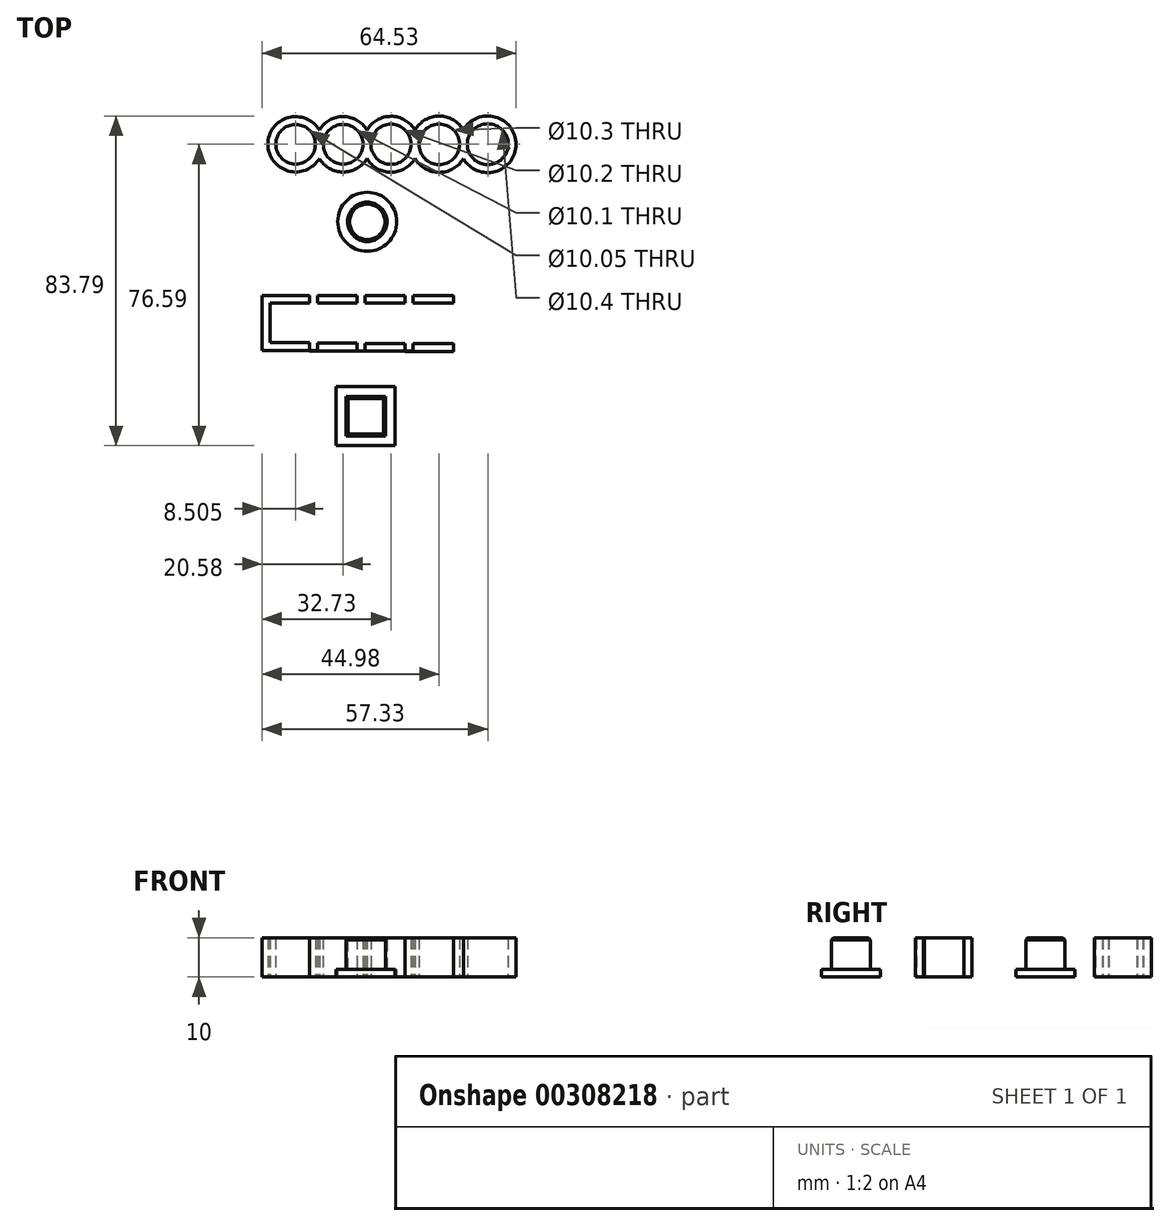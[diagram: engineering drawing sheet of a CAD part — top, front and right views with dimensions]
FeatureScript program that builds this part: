
annotation { "Feature Type Name" : "Feature", "Feature Type Description" : "" }
export const myFeature = defineFeature(function(context is Context, id is Id, definition is map)
    precondition{}
    {
        {
            var Q0;
            Q0=qCreatedBy(makeId("Top.planeOp"),FACE);
            var sketch = newSketch(context, id + "F0", { "sketchPlane" : qUnion([Q0])});
            skLineSegment(sketch, "E0", {"start": v(-24.23, 14.63) * mm, "end": v(24.6, 14.63) * mm, "construction": true});
            skPoint(sketch, "E1", {"position": v(-12.15, 14.63) * mm});
            skPoint(sketch, "E2", {"position": v(0, 14.63) * mm});
            skPoint(sketch, "E3", {"position": v(12.25, 14.63) * mm});
            skCircle(sketch, "E4", {"center": v(-24.23, 14.63) * mm, "radius": 5.03 * mm});
            skCircle(sketch, "E5", {"center": v(24.6, 14.63) * mm, "radius": 5.2 * mm});
            skCircle(sketch, "E6", {"center": v(-12.15, 14.63) * mm, "radius": 5.05 * mm});
            skCircle(sketch, "E7", {"center": v(0, 14.63) * mm, "radius": 5.1 * mm});
            skCircle(sketch, "E8", {"center": v(12.25, 14.63) * mm, "radius": 5.15 * mm});
            skCircle(sketch, "E9", {"center": v(-24.23, 14.63) * mm, "radius": 7.03 * mm});
            skCircle(sketch, "E10", {"center": v(-12.15, 14.63) * mm, "radius": 7.05 * mm});
            skCircle(sketch, "E11", {"center": v(0, 14.63) * mm, "radius": 7.1 * mm});
            skCircle(sketch, "E12", {"center": v(12.25, 14.63) * mm, "radius": 7.15 * mm});
            skCircle(sketch, "E13", {"center": v(24.6, 14.63) * mm, "radius": 7.2 * mm});
            skCircle(sketch, "E14", {"center": v(-6.02, -5.07) * mm, "radius": 7.5 * mm});
            skCircle(sketch, "E15", {"center": v(-6.02, -5.07) * mm, "radius": 5 * mm});
            skLineSegment(sketch, "E16", {"start": v(-34.81, -23.75) * mm, "end": v(32.17, -23.75) * mm, "construction": true});
            skPoint(sketch, "E17", {"position": v(-25.7, -30.78) * mm});
            skPoint(sketch, "E18", {"position": v(-13.63, -30.8) * mm});
            skPoint(sketch, "E19", {"position": v(10.77, -30.9) * mm});
            skLineSegment(sketch, "E20.bottom", {"start": v(-30.73, -25.75) * mm, "end": v(-20.68, -25.75) * mm});
            skLineSegment(sketch, "E20.top", {"start": v(-30.73, -35.8) * mm, "end": v(-20.68, -35.8) * mm});
            skLineSegment(sketch, "E20.left", {"start": v(-30.73, -25.75) * mm, "end": v(-30.73, -35.8) * mm});
            skLineSegment(sketch, "E20.right", {"start": v(-20.68, -25.75) * mm, "end": v(-20.68, -35.8) * mm});
            skLineSegment(sketch, "E21.bottom", {"start": v(-32.73, -23.75) * mm, "end": v(-18.68, -23.75) * mm});
            skLineSegment(sketch, "E21.top", {"start": v(-32.73, -37.8) * mm, "end": v(-18.68, -37.8) * mm});
            skLineSegment(sketch, "E21.left", {"start": v(-32.73, -23.75) * mm, "end": v(-32.73, -37.8) * mm});
            skLineSegment(sketch, "E21.right", {"start": v(-18.68, -23.75) * mm, "end": v(-18.68, -37.8) * mm});
            skLineSegment(sketch, "E22.bottom", {"start": v(-8.58, -35.85) * mm, "end": v(-18.68, -35.85) * mm});
            skLineSegment(sketch, "E22.top", {"start": v(-8.58, -25.75) * mm, "end": v(-18.68, -25.75) * mm});
            skLineSegment(sketch, "E22.left", {"start": v(-8.58, -35.85) * mm, "end": v(-8.58, -25.75) * mm});
            skLineSegment(sketch, "E22.right", {"start": v(-18.68, -35.85) * mm, "end": v(-18.68, -25.75) * mm});
            skLineSegment(sketch, "E23.bottom", {"start": v(-6.58, -23.75) * mm, "end": v(-20.68, -23.75) * mm});
            skLineSegment(sketch, "E23.top", {"start": v(-6.58, -37.85) * mm, "end": v(-20.68, -37.85) * mm});
            skLineSegment(sketch, "E23.left", {"start": v(-6.58, -23.75) * mm, "end": v(-6.58, -37.85) * mm});
            skLineSegment(sketch, "E23.right", {"start": v(-20.68, -23.75) * mm, "end": v(-20.68, -37.85) * mm});
            skLineSegment(sketch, "E24.bottom", {"start": v(-6.58, -25.75) * mm, "end": v(3.62, -25.75) * mm});
            skLineSegment(sketch, "E24.top", {"start": v(-6.58, -35.95) * mm, "end": v(3.62, -35.95) * mm});
            skLineSegment(sketch, "E24.left", {"start": v(-6.58, -25.75) * mm, "end": v(-6.58, -35.95) * mm});
            skLineSegment(sketch, "E24.right", {"start": v(3.62, -25.75) * mm, "end": v(3.62, -35.95) * mm});
            skPoint(sketch, "E24.middle", {"position": v(-1.48, -30.85) * mm});
            skLineSegment(sketch, "E25.bottom", {"start": v(-8.58, -23.75) * mm, "end": v(5.62, -23.75) * mm});
            skLineSegment(sketch, "E25.top", {"start": v(-8.58, -37.95) * mm, "end": v(5.62, -37.95) * mm});
            skLineSegment(sketch, "E25.left", {"start": v(-8.58, -23.75) * mm, "end": v(-8.58, -37.95) * mm});
            skLineSegment(sketch, "E25.right", {"start": v(5.62, -23.75) * mm, "end": v(5.62, -37.95) * mm});
            skLineSegment(sketch, "E26.bottom", {"start": v(15.92, -25.75) * mm, "end": v(5.62, -25.75) * mm});
            skLineSegment(sketch, "E26.top", {"start": v(15.92, -36.05) * mm, "end": v(5.62, -36.05) * mm});
            skLineSegment(sketch, "E26.left", {"start": v(15.92, -25.75) * mm, "end": v(15.92, -36.05) * mm});
            skLineSegment(sketch, "E26.right", {"start": v(5.62, -25.75) * mm, "end": v(5.62, -36.05) * mm});
            skLineSegment(sketch, "E27.bottom", {"start": v(17.92, -23.75) * mm, "end": v(3.62, -23.75) * mm});
            skLineSegment(sketch, "E27.top", {"start": v(17.92, -38.05) * mm, "end": v(3.62, -38.05) * mm});
            skLineSegment(sketch, "E27.left", {"start": v(17.92, -23.75) * mm, "end": v(17.92, -38.05) * mm});
            skLineSegment(sketch, "E27.right", {"start": v(3.62, -23.75) * mm, "end": v(3.62, -38.05) * mm});
            skPoint(sketch, "E28", {"position": v(23.12, -30.95) * mm});
            skLineSegment(sketch, "E29.bottom", {"start": v(28.32, -25.75) * mm, "end": v(17.92, -25.75) * mm});
            skLineSegment(sketch, "E29.top", {"start": v(28.32, -36.15) * mm, "end": v(17.92, -36.15) * mm});
            skLineSegment(sketch, "E29.left", {"start": v(28.32, -25.75) * mm, "end": v(28.32, -36.15) * mm});
            skLineSegment(sketch, "E29.right", {"start": v(17.92, -25.75) * mm, "end": v(17.92, -36.15) * mm});
            skLineSegment(sketch, "E30.bottom", {"start": v(30.32, -23.75) * mm, "end": v(15.92, -23.75) * mm});
            skLineSegment(sketch, "E30.top", {"start": v(30.32, -38.15) * mm, "end": v(15.92, -38.15) * mm});
            skLineSegment(sketch, "E30.left", {"start": v(30.32, -23.75) * mm, "end": v(30.32, -38.15) * mm});
            skLineSegment(sketch, "E30.right", {"start": v(15.92, -23.75) * mm, "end": v(15.92, -38.15) * mm});
            skPoint(sketch, "E31", {"position": v(-6.42, -54.46) * mm});
            skLineSegment(sketch, "E32.bottom", {"start": v(-11.42, -49.46) * mm, "end": v(-1.42, -49.46) * mm});
            skLineSegment(sketch, "E32.top", {"start": v(-11.42, -59.46) * mm, "end": v(-1.42, -59.46) * mm});
            skLineSegment(sketch, "E32.left", {"start": v(-11.42, -49.46) * mm, "end": v(-11.42, -59.46) * mm});
            skLineSegment(sketch, "E32.right", {"start": v(-1.42, -49.46) * mm, "end": v(-1.42, -59.46) * mm});
            skLineSegment(sketch, "E33.bottom", {"start": v(-13.92, -46.96) * mm, "end": v(1.08, -46.96) * mm});
            skLineSegment(sketch, "E33.top", {"start": v(-13.92, -61.96) * mm, "end": v(1.08, -61.96) * mm});
            skLineSegment(sketch, "E33.left", {"start": v(-13.92, -46.96) * mm, "end": v(-13.92, -61.96) * mm});
            skLineSegment(sketch, "E33.right", {"start": v(1.08, -46.96) * mm, "end": v(1.08, -61.96) * mm});
            skSolve(sketch);
        }
        {
            var Q0;
            {var subQ0=sQuery(id+"F0.wireOp",EDGE,"E4");Q0=makeQuery(id+"F0.imprint","IMPRINT",FACE,{"disambiguationData":[TD([[makeQuery(id+"F0.imprint","IMPRINT",EDGE,{"derivedFrom":subQ0}),-1.0]])]});}
            var Q1;
            {var subQ0=sQuery(id+"F0.wireOp",EDGE,"E9");var subQ1=sQuery(id+"F0.wireOp",EDGE,"E6");var subQ2=makeQuery(id+"F0.imprint","INTERSECT",VERTEX,{"derivedFrom":[subQ1,subQ0]});Q1=makeQuery(id+"F0.imprint","IMPRINT",FACE,{"disambiguationData":[TD([[makeQuery(id+"F0.imprint","IMPRINT",EDGE,{"disambiguationData":[TD([[subQ2,1.0]])],"derivedFrom":subQ1}),-1.0]])]});}
            var Q2;
            {var subQ0=sQuery(id+"F0.wireOp",EDGE,"E10");var subQ1=sQuery(id+"F0.wireOp",EDGE,"E7");var subQ2=makeQuery(id+"F0.imprint","INTERSECT",VERTEX,{"derivedFrom":[subQ1,subQ0]});Q2=makeQuery(id+"F0.imprint","IMPRINT",FACE,{"disambiguationData":[TD([[makeQuery(id+"F0.imprint","IMPRINT",EDGE,{"disambiguationData":[TD([[subQ2,1.0]])],"derivedFrom":subQ1}),-1.0]])]});}
            var Q3;
            {var subQ0=sQuery(id+"F0.wireOp",EDGE,"E11");var subQ1=sQuery(id+"F0.wireOp",EDGE,"E8");var subQ2=makeQuery(id+"F0.imprint","INTERSECT",VERTEX,{"derivedFrom":[subQ1,subQ0]});Q3=makeQuery(id+"F0.imprint","IMPRINT",FACE,{"disambiguationData":[TD([[makeQuery(id+"F0.imprint","IMPRINT",EDGE,{"disambiguationData":[TD([[subQ2,1.0]])],"derivedFrom":subQ1}),-1.0]])]});}
            var Q4;
            {var subQ0=sQuery(id+"F0.wireOp",EDGE,"E5");Q4=makeQuery(id+"F0.imprint","IMPRINT",FACE,{"disambiguationData":[TD([[makeQuery(id+"F0.imprint","IMPRINT",EDGE,{"derivedFrom":subQ0}),-1.0]])]});}
            var Q5;
            {var subQ0=sQuery(id+"F0.wireOp",EDGE,"E12");var subQ1=makeQuery(id+"F0.imprint","INTERSECT",VERTEX,{"derivedFrom":[sQuery(id+"F0.wireOp",EDGE,"E5"),subQ0]});Q5=makeQuery(id+"F0.imprint","IMPRINT",FACE,{"disambiguationData":[TD([[makeQuery(id+"F0.imprint","IMPRINT",EDGE,{"disambiguationData":[TD([[subQ1,-1.0]])],"derivedFrom":subQ0}),1.0]])]});}
            var Q6;
            {var subQ0=sQuery(id+"F0.wireOp",EDGE,"E12");var subQ1=sQuery(id+"F0.wireOp",EDGE,"E11");var subQ2=makeQuery(id+"F0.imprint","INTERSECT",VERTEX,{"disambiguationData":[OD(0.0)],"derivedFrom":[subQ1,subQ0]});Q6=makeQuery(id+"F0.imprint","IMPRINT",FACE,{"disambiguationData":[TD([[makeQuery(id+"F0.imprint","IMPRINT",EDGE,{"disambiguationData":[TD([[subQ2,1.0]])],"derivedFrom":subQ1}),1.0]])]});}
            var Q7;
            {var subQ0=sQuery(id+"F0.wireOp",EDGE,"E11");var subQ1=sQuery(id+"F0.wireOp",EDGE,"E10");var subQ2=makeQuery(id+"F0.imprint","INTERSECT",VERTEX,{"disambiguationData":[OD(0.0)],"derivedFrom":[subQ1,subQ0]});Q7=makeQuery(id+"F0.imprint","IMPRINT",FACE,{"disambiguationData":[TD([[makeQuery(id+"F0.imprint","IMPRINT",EDGE,{"disambiguationData":[TD([[subQ2,1.0]])],"derivedFrom":subQ1}),1.0]])]});}
            var Q8;
            {var subQ0=sQuery(id+"F0.wireOp",EDGE,"E10");var subQ1=sQuery(id+"F0.wireOp",EDGE,"E9");var subQ2=makeQuery(id+"F0.imprint","INTERSECT",VERTEX,{"disambiguationData":[OD(0.0)],"derivedFrom":[subQ1,subQ0]});Q8=makeQuery(id+"F0.imprint","IMPRINT",FACE,{"disambiguationData":[TD([[makeQuery(id+"F0.imprint","IMPRINT",EDGE,{"disambiguationData":[TD([[subQ2,1.0]])],"derivedFrom":subQ1}),1.0]])]});}
            var Q9;
            {var subQ0=sQuery(id+"F0.wireOp",EDGE,"E9");var subQ1=sQuery(id+"F0.wireOp",EDGE,"E6");var subQ2=makeQuery(id+"F0.imprint","INTERSECT",VERTEX,{"derivedFrom":[subQ1,subQ0]});Q9=makeQuery(id+"F0.imprint","IMPRINT",FACE,{"disambiguationData":[TD([[makeQuery(id+"F0.imprint","IMPRINT",EDGE,{"disambiguationData":[TD([[subQ2,-1.0]])],"derivedFrom":subQ1}),-1.0]])]});}
            var Q10;
            {var subQ0=sQuery(id+"F0.wireOp",EDGE,"E10");var subQ1=sQuery(id+"F0.wireOp",EDGE,"E7");var subQ2=makeQuery(id+"F0.imprint","INTERSECT",VERTEX,{"derivedFrom":[subQ1,subQ0]});Q10=makeQuery(id+"F0.imprint","IMPRINT",FACE,{"disambiguationData":[TD([[makeQuery(id+"F0.imprint","IMPRINT",EDGE,{"disambiguationData":[TD([[subQ2,-1.0]])],"derivedFrom":subQ1}),-1.0]])]});}
            var Q11;
            {var subQ0=sQuery(id+"F0.wireOp",EDGE,"E11");var subQ1=sQuery(id+"F0.wireOp",EDGE,"E8");var subQ2=makeQuery(id+"F0.imprint","INTERSECT",VERTEX,{"derivedFrom":[subQ1,subQ0]});Q11=makeQuery(id+"F0.imprint","IMPRINT",FACE,{"disambiguationData":[TD([[makeQuery(id+"F0.imprint","IMPRINT",EDGE,{"disambiguationData":[TD([[subQ2,-1.0]])],"derivedFrom":subQ1}),-1.0]])]});}
            var Q12;
            Q12=makeQuery(id+"F0.imprint","IMPRINT",FACE,{"disambiguationData":[TD([[makeQuery(id+"F0.imprint","IMPRINT",EDGE,{"derivedFrom":sQuery(id+"F0.wireOp",EDGE,"E15")}),1.0]])]});
            var Q13;
            {var subQ2=sQuery(id+"F0.wireOp",EDGE,"E20.bottom");Q13=makeQuery(id+"F0.imprint","IMPRINT",FACE,{"disambiguationData":[TD([[makeQuery(id+"F0.imprint","IMPRINT",EDGE,{"derivedFrom":subQ2}),1.0]])]});}
            var Q14;
            {var subQ0=sQuery(id+"F0.wireOp",EDGE,"E22.right");Q14=makeQuery(id+"F0.imprint","IMPRINT",FACE,{"disambiguationData":[TD([[makeQuery(id+"F0.imprint","IMPRINT",EDGE,{"derivedFrom":subQ0}),1.0]])]});}
            var Q15;
            {var subQ3=sQuery(id+"F0.wireOp",EDGE,"E22.top");Q15=makeQuery(id+"F0.imprint","IMPRINT",FACE,{"disambiguationData":[TD([[makeQuery(id+"F0.imprint","IMPRINT",EDGE,{"derivedFrom":subQ3}),-1.0]])]});}
            var Q16;
            {var subQ0=sQuery(id+"F0.wireOp",EDGE,"E22.bottom");Q16=makeQuery(id+"F0.imprint","IMPRINT",FACE,{"disambiguationData":[TD([[makeQuery(id+"F0.imprint","IMPRINT",EDGE,{"derivedFrom":subQ0}),1.0]])]});}
            var Q17;
            {var subQ3=sQuery(id+"F0.wireOp",EDGE,"E24.left");Q17=makeQuery(id+"F0.imprint","IMPRINT",FACE,{"disambiguationData":[TD([[makeQuery(id+"F0.imprint","IMPRINT",EDGE,{"derivedFrom":subQ3}),-1.0]])]});}
            var Q18;
            {var subQ3=sQuery(id+"F0.wireOp",EDGE,"E24.bottom");Q18=makeQuery(id+"F0.imprint","IMPRINT",FACE,{"disambiguationData":[TD([[makeQuery(id+"F0.imprint","IMPRINT",EDGE,{"derivedFrom":subQ3}),1.0]])]});}
            var Q19;
            {var subQ0=sQuery(id+"F0.wireOp",EDGE,"E24.top");Q19=makeQuery(id+"F0.imprint","IMPRINT",FACE,{"disambiguationData":[TD([[makeQuery(id+"F0.imprint","IMPRINT",EDGE,{"derivedFrom":subQ0}),-1.0]])]});}
            var Q20;
            {var subQ0=sQuery(id+"F0.wireOp",EDGE,"E26.right");Q20=makeQuery(id+"F0.imprint","IMPRINT",FACE,{"disambiguationData":[TD([[makeQuery(id+"F0.imprint","IMPRINT",EDGE,{"derivedFrom":subQ0}),-1.0]])]});}
            var Q21;
            {var subQ3=sQuery(id+"F0.wireOp",EDGE,"E26.bottom");Q21=makeQuery(id+"F0.imprint","IMPRINT",FACE,{"disambiguationData":[TD([[makeQuery(id+"F0.imprint","IMPRINT",EDGE,{"derivedFrom":subQ3}),-1.0]])]});}
            var Q22;
            {var subQ5=sQuery(id+"F0.wireOp",EDGE,"E26.top");Q22=makeQuery(id+"F0.imprint","IMPRINT",FACE,{"disambiguationData":[TD([[makeQuery(id+"F0.imprint","IMPRINT",EDGE,{"derivedFrom":subQ5}),1.0]])]});}
            var Q23;
            {var subQ0=sQuery(id+"F0.wireOp",EDGE,"E29.right");Q23=makeQuery(id+"F0.imprint","IMPRINT",FACE,{"disambiguationData":[TD([[makeQuery(id+"F0.imprint","IMPRINT",EDGE,{"derivedFrom":subQ0}),-1.0]])]});}
            var Q24;
            {var subQ0=sQuery(id+"F0.wireOp",EDGE,"E29.bottom");Q24=makeQuery(id+"F0.imprint","IMPRINT",FACE,{"disambiguationData":[TD([[makeQuery(id+"F0.imprint","IMPRINT",EDGE,{"derivedFrom":subQ0}),-1.0]])]});}
            var Q25;
            Q25=makeQuery(id+"F0.imprint","IMPRINT",FACE,{"disambiguationData":[TD([[makeQuery(id+"F0.imprint","IMPRINT",EDGE,{"derivedFrom":sQuery(id+"F0.wireOp",EDGE,"E32.bottom")}),-1.0]])]});
            extrude(context, id + "F1", {"entities" : qUnion([Q0, Q1, Q2, Q3, Q4, Q5, Q6, Q7, Q8, Q9, Q10, Q11, Q12, Q13, Q14, Q15, Q16, Q17, Q18, Q19, Q20, Q21, Q22, Q23, Q24, Q25]), "depth" : 10 * mm, "offsetDistance" : 25 * mm});
        }
        {
            var Q0;
            Q0=makeQuery(id+"F0.imprint","IMPRINT",FACE,{"disambiguationData":[TD([[makeQuery(id+"F0.imprint","IMPRINT",EDGE,{"derivedFrom":sQuery(id+"F0.wireOp",EDGE,"E14")}),1.0]])]});
            var Q1;
            Q1=makeQuery(id+"F0.imprint","IMPRINT",FACE,{"disambiguationData":[TD([[makeQuery(id+"F0.imprint","IMPRINT",EDGE,{"derivedFrom":sQuery(id+"F0.wireOp",EDGE,"E32.bottom")}),1.0]])]});
            extrude(context, id + "F2", {"entities" : qUnion([Q0, Q1]), "operationType" : NewBodyOperationType.ADD, "depth" : 2 * mm, "offsetDistance" : 25 * mm});
        }
        {
            var Q0;
            Q0=makeQuery(id+"F1.opExtrude","CAP_EDGE",EDGE,{"disambiguationData":[OSD([sQuery(id+"F0.wireOp",EDGE,"E15")])],"isStart":false});
            var Q1;
            Q1=makeQuery(id+"F1.opExtrude","CAP_FACE",FACE,{"disambiguationData":[OSD([sQuery(id+"F0.wireOp",EDGE,"E32.bottom"),sQuery(id+"F0.wireOp",EDGE,"E32.top"),sQuery(id+"F0.wireOp",EDGE,"E32.left"),sQuery(id+"F0.wireOp",EDGE,"E32.right")])],"isStart":false});
            chamfer(context, id + "F3", {"entities" : qUnion([Q0, Q1]), "width" : 0.5 * mm, "tangentPropagation" : true});
        }
    });
